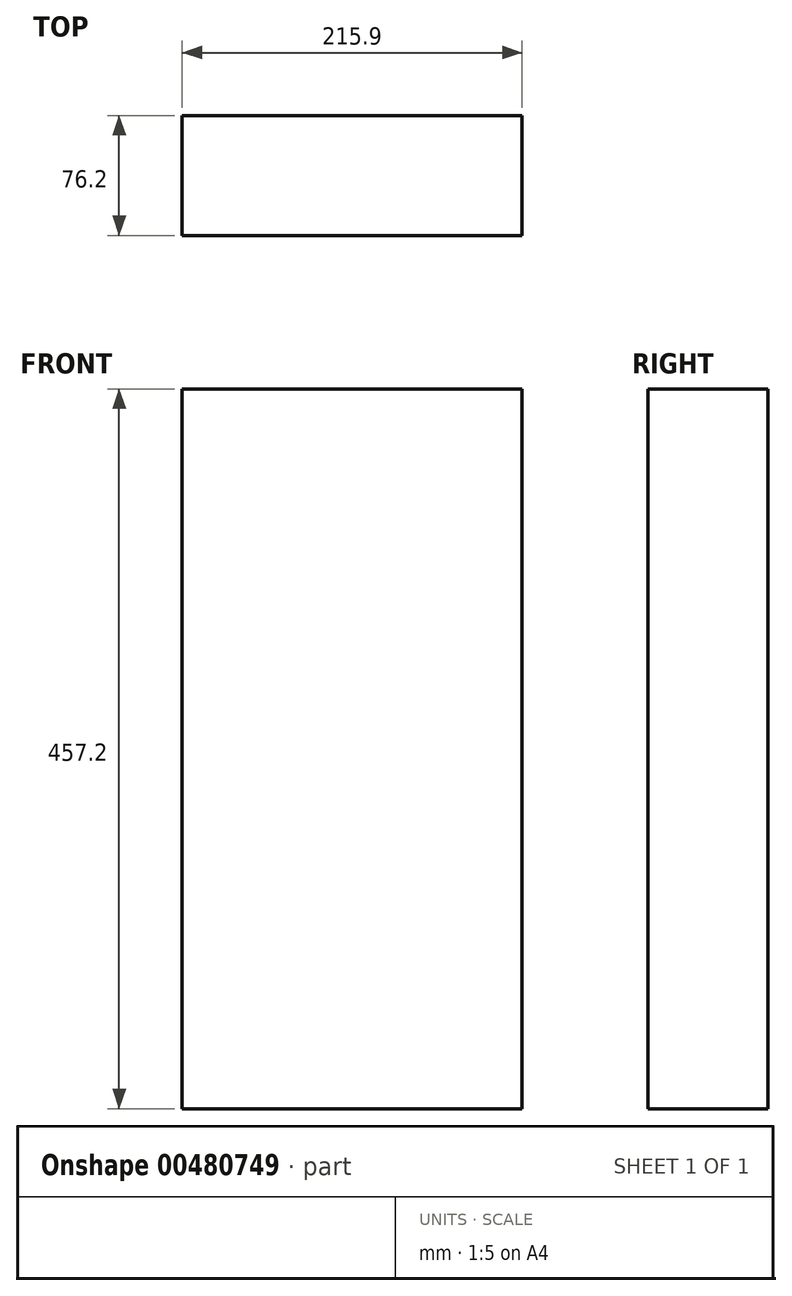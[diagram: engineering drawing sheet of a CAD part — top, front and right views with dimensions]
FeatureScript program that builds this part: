
annotation { "Feature Type Name" : "Feature", "Feature Type Description" : "" }
export const myFeature = defineFeature(function(context is Context, id is Id, definition is map)
    precondition{}
    {
        {
            var Q0;
            Q0=qCreatedBy(makeId("Front.planeOp"),FACE);
            var sketch = newSketch(context, id + "F0", { "sketchPlane" : qUnion([Q0])});
            skLineSegment(sketch, "E0.bottom", {"start": v(-76.18, 146.5) * mm, "end": v(139.72, 146.5) * mm});
            skLineSegment(sketch, "E0.top", {"start": v(-76.18, -310.7) * mm, "end": v(139.72, -310.7) * mm});
            skLineSegment(sketch, "E0.left", {"start": v(-76.18, 146.5) * mm, "end": v(-76.18, -310.7) * mm});
            skLineSegment(sketch, "E0.right", {"start": v(139.72, 146.5) * mm, "end": v(139.72, -310.7) * mm});
            skSolve(sketch);
        }
        {
            var Q0;
            Q0=makeQuery(id+"F0.imprint","IMPRINT",FACE,{"disambiguationData":[TD([[makeQuery(id+"F0.imprint","IMPRINT",EDGE,{"derivedFrom":sQuery(id+"F0.wireOp",EDGE,"E0.bottom")}),-1.0]])]});
            extrude(context, id + "F1", {"entities" : qUnion([Q0]), "depth" : 76.2 * mm});
        }
    });
